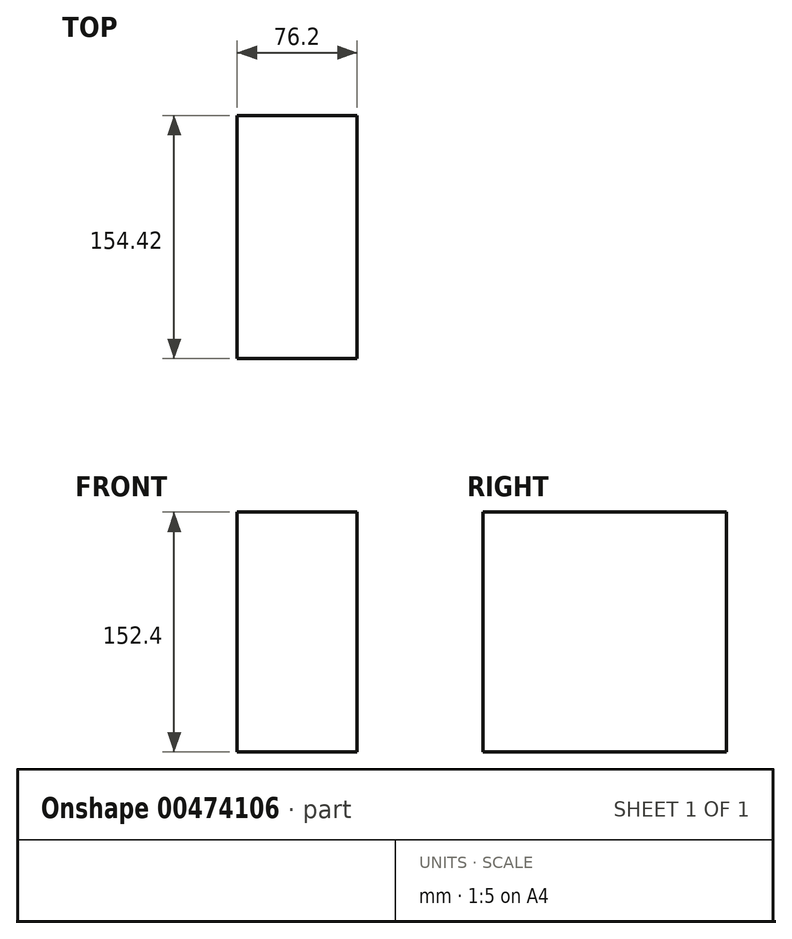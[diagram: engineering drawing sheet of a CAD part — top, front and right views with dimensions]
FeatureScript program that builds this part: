
annotation { "Feature Type Name" : "Feature", "Feature Type Description" : "" }
export const myFeature = defineFeature(function(context is Context, id is Id, definition is map)
    precondition{}
    {
        {
            var Q0;
            Q0=qCreatedBy(makeId("Top.planeOp"),FACE);
            var sketch = newSketch(context, id + "F0", { "sketchPlane" : qUnion([Q0])});
            skLineSegment(sketch, "E0.bottom", {"start": v(38.1, 77.2) * mm, "end": v(-38.1, 77.2) * mm});
            skLineSegment(sketch, "E0.top", {"start": v(38.1, -77.2) * mm, "end": v(-38.1, -77.2) * mm});
            skLineSegment(sketch, "E0.left", {"start": v(38.1, 77.2) * mm, "end": v(38.1, -77.2) * mm});
            skLineSegment(sketch, "E0.right", {"start": v(-38.1, 77.2) * mm, "end": v(-38.1, -77.2) * mm});
            skPoint(sketch, "E0.middle", {"position": v(0, 0) * mm});
            skSolve(sketch);
        }
        {
            var Q0;
            Q0 = qSketchRegion(id + "F0", true);
            extrude(context, id + "F1", {"entities" : qUnion([Q0]), "depth" : 152.4 * mm});
        }
    });
